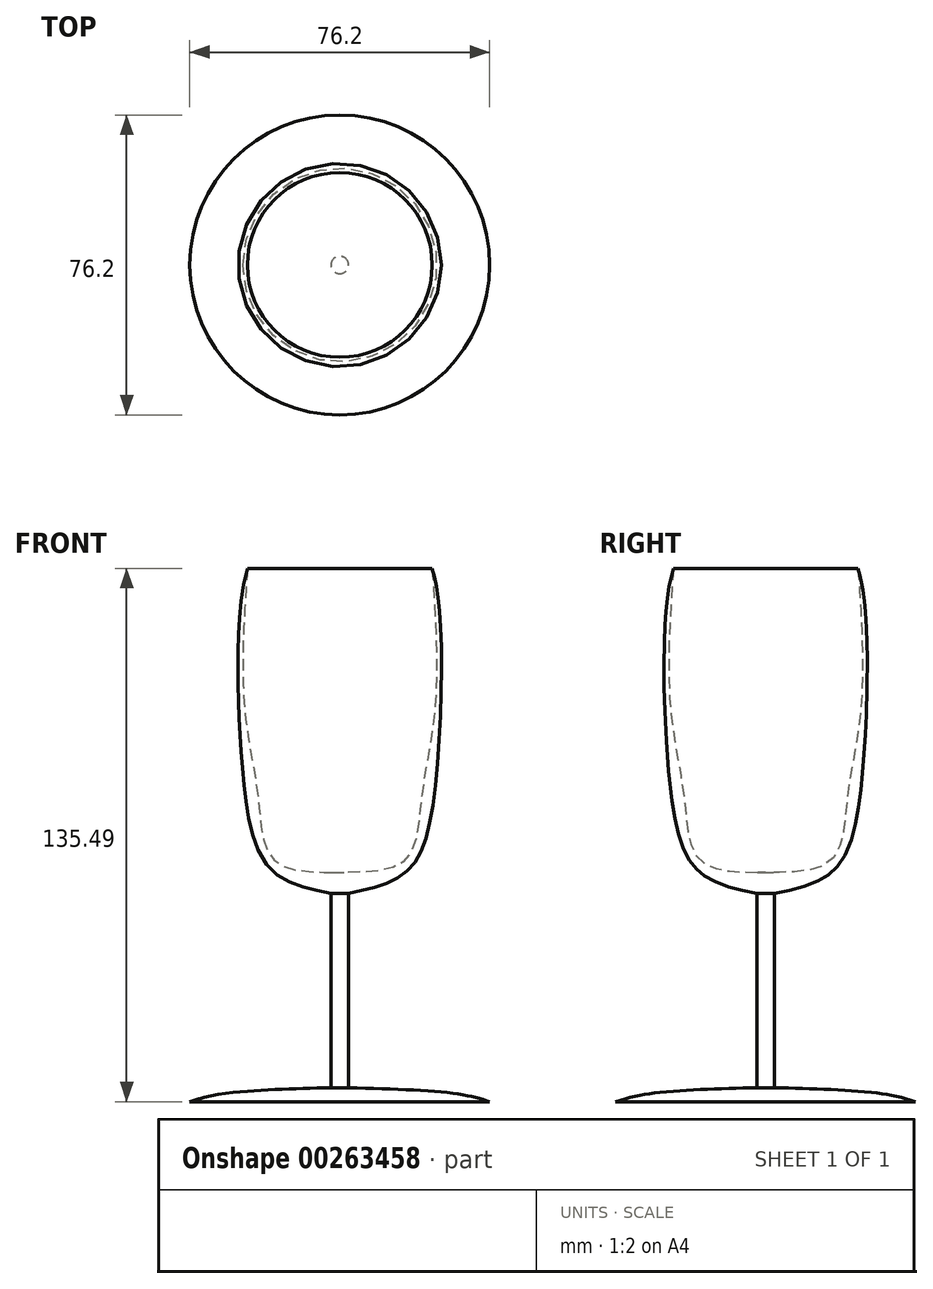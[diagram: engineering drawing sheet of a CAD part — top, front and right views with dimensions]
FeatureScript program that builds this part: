
annotation { "Feature Type Name" : "Feature", "Feature Type Description" : "" }
export const myFeature = defineFeature(function(context is Context, id is Id, definition is map)
    precondition{}
    {
        {
            var Q0;
            Q0=qCreatedBy(makeId("Front.planeOp"),FACE);
            var sketch = newSketch(context, id + "F0", { "sketchPlane" : qUnion([Q0])});
            skLineSegment(sketch, "E0", {"start": v(0, 0) * mm, "end": v(-38.1, 0) * mm});
            skFitSpline(sketch, "E1", {"points": [v(-38.1, 0) * mm, v(-29.78, 2) * mm, v(-2.22, 3.56) * mm], "startDerivative": vector(19.75, 6.16) * mm, "endDerivative": vector(49.21, 1.4) * mm});
            skLineSegment(sketch, "E2", {"start": v(-2.22, 3.56) * mm, "end": v(-2.22, 52.9) * mm});
            skFitSpline(sketch, "E3", {"points": [v(-2.22, 52.9) * mm, v(-16.74, 58.26) * mm, v(-23.87, 76.88) * mm, v(-25.45, 123.6) * mm, v(-23.47, 135.49) * mm], "startDerivative": vector(-77.64, 16.36) * mm, "endDerivative": vector(12.59, 49.87) * mm});
            skFitSpline(sketch, "E4", {"points": [v(-23.47, 135.49) * mm, v(-24.25, 100.64) * mm, v(-20.7, 76.88) * mm, v(-16.74, 61.43) * mm, v(0, 58.26) * mm], "startDerivative": vector(-8.02, -117.2) * mm, "endDerivative": vector(92.32, 0.41) * mm});
            skLineSegment(sketch, "E5", {"start": v(0, 58.26) * mm, "end": v(0, 0) * mm});
            skSolve(sketch);
        }
        {
            var Q0;
            Q0=makeQuery(id+"F0.imprint","IMPRINT",FACE,{"disambiguationData":[TD([[makeQuery(id+"F0.imprint","IMPRINT",EDGE,{"derivedFrom":sQuery(id+"F0.wireOp",EDGE,"E0")}),-1.0]])]});
            var Q1;
            Q1=sQuery(id+"F0.wireOp",EDGE,"E5");
            revolve(context, id + "F1", {"entities" : qUnion([Q0]), "axis" : qUnion([Q1]), "revolveType" : RevolveType.FULL});
        }
    });
